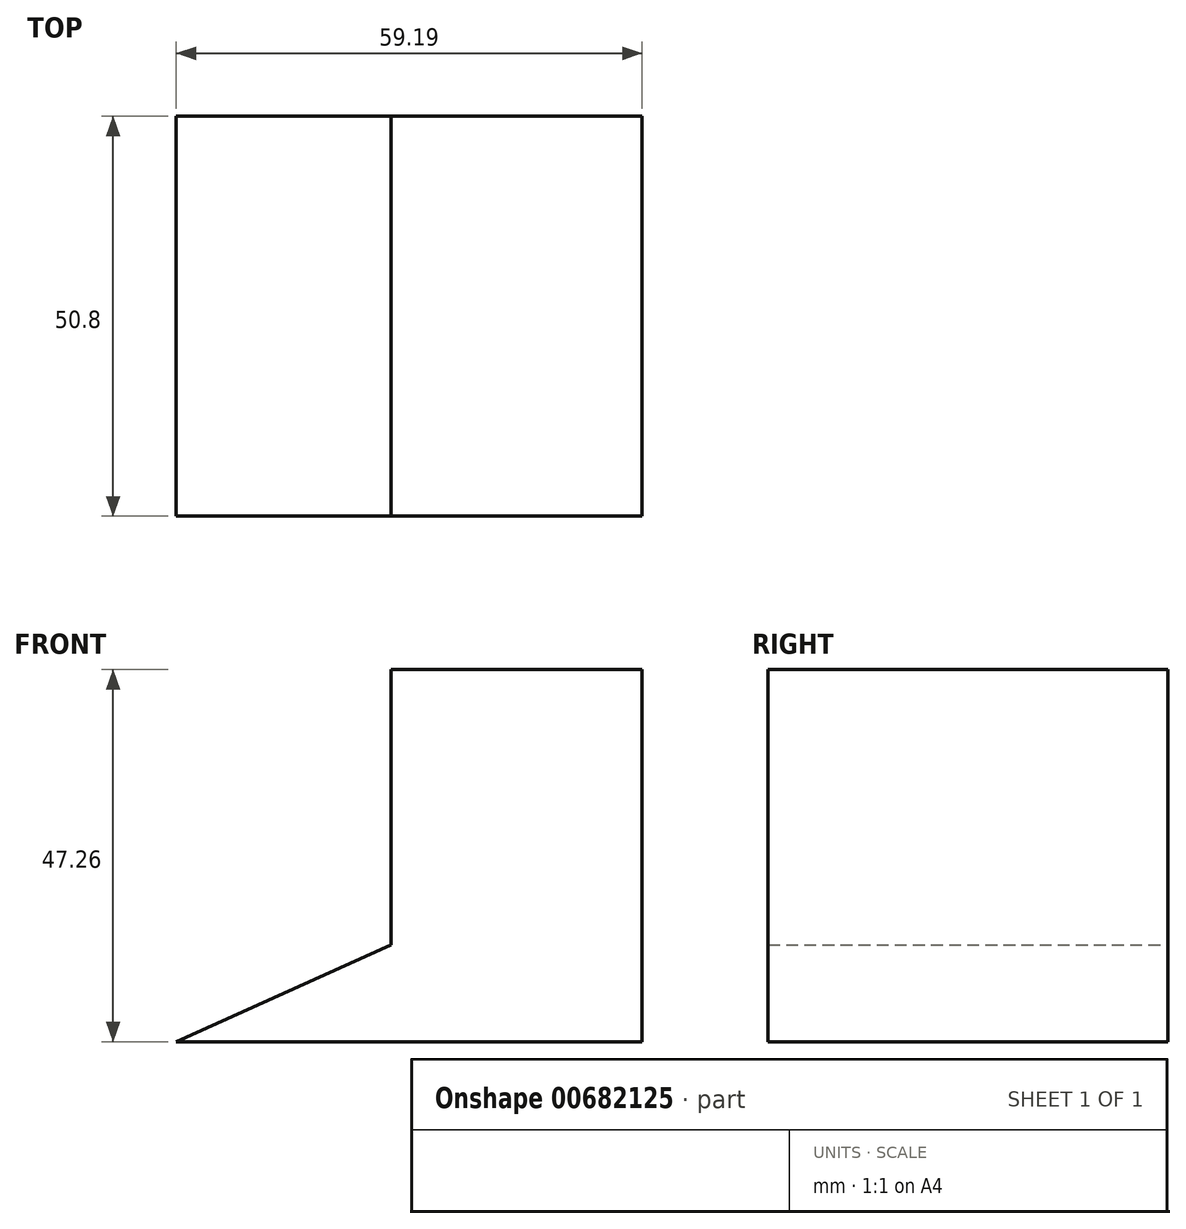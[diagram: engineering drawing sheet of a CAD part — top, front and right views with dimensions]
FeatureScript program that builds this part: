
annotation { "Feature Type Name" : "Feature", "Feature Type Description" : "" }
export const myFeature = defineFeature(function(context is Context, id is Id, definition is map)
    precondition{}
    {
        {
            var Q0;
            Q0=qCreatedBy(makeId("Front.planeOp"),FACE);
            var sketch = newSketch(context, id + "F0", { "sketchPlane" : qUnion([Q0])});
            skLineSegment(sketch, "E0", {"start": v(11.93, 0) * mm, "end": v(-45.92, 0) * mm});
            skLineSegment(sketch, "E1", {"start": v(-45.92, 0) * mm, "end": v(-18.62, 12.32) * mm});
            skLineSegment(sketch, "E2", {"start": v(-18.62, 12.32) * mm, "end": v(-18.62, 47.26) * mm});
            skLineSegment(sketch, "E3", {"start": v(-18.62, 47.26) * mm, "end": v(13.27, 47.26) * mm});
            skLineSegment(sketch, "E4", {"start": v(13.27, 47.26) * mm, "end": v(13.27, 0) * mm});
            skLineSegment(sketch, "E5", {"start": v(11.93, 0) * mm, "end": v(13.27, 0) * mm});
            skLineSegment(sketch, "E6", {"start": v(27.43, 10.87) * mm, "end": v(25.13, 13.17) * mm});
            skSolve(sketch);
        }
        {
            var Q0;
            Q0 = qSketchRegion(id + "F0", true);
            extrude(context, id + "F1", {"entities" : qUnion([Q0]), "depth" : 50.8 * mm, "offsetDistance" : 25.4 * mm});
        }
    });
